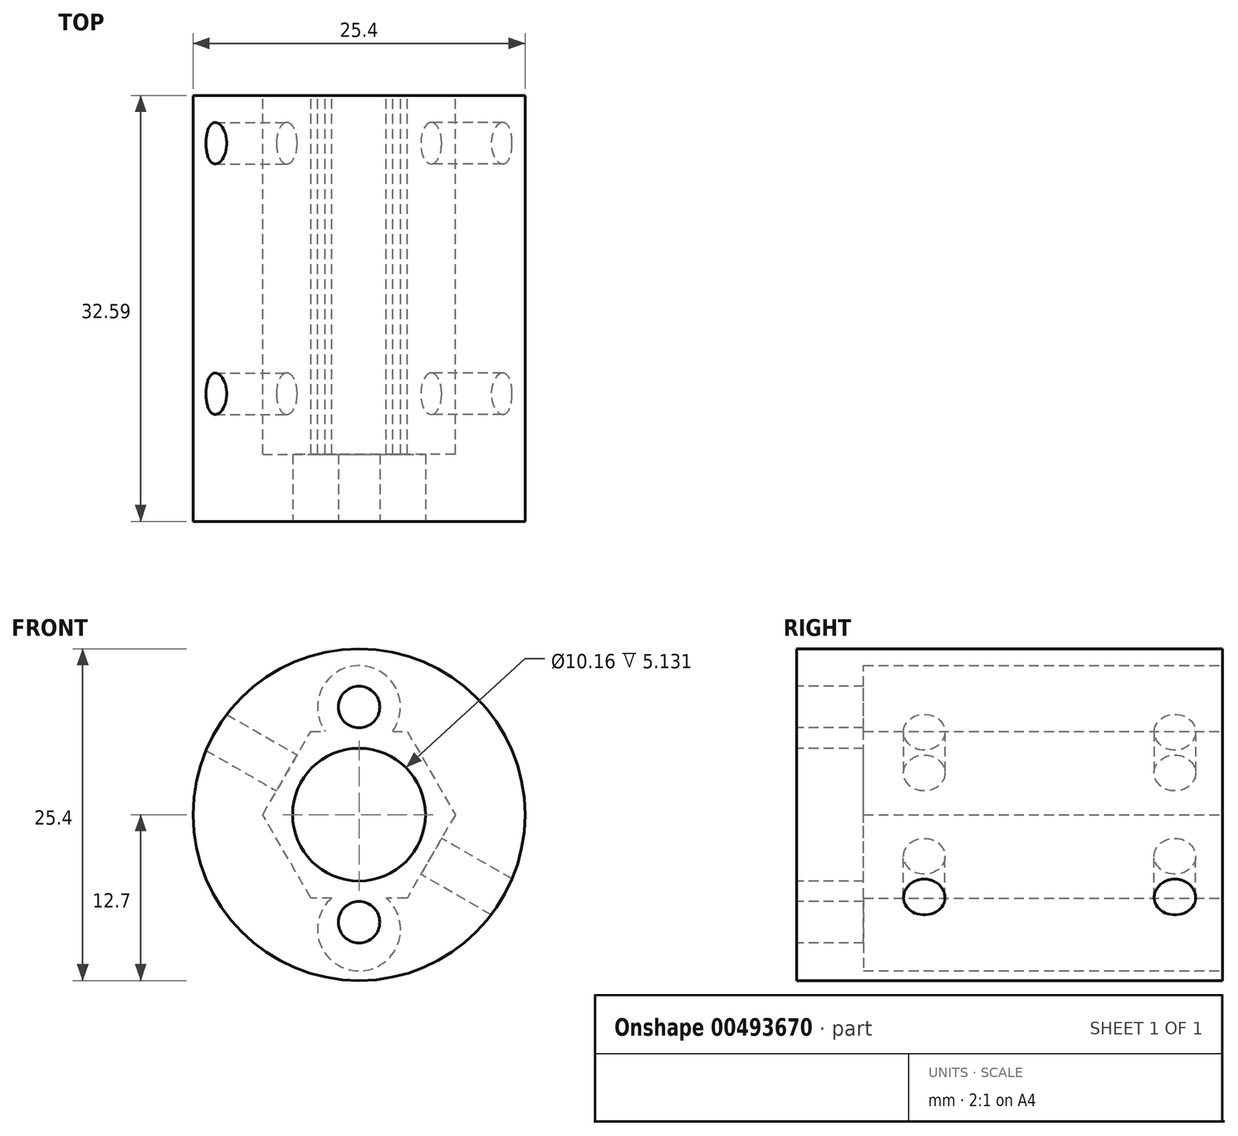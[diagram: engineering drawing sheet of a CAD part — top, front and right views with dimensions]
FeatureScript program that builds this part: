
annotation { "Feature Type Name" : "Feature", "Feature Type Description" : "" }
export const myFeature = defineFeature(function(context is Context, id is Id, definition is map)
    precondition{}
    {
        {
            var Q0;
            Q0=qCreatedBy(makeId("Front.planeOp"),FACE);
            var sketch = newSketch(context, id + "F0", { "sketchPlane" : qUnion([Q0])});
            skCircle(sketch, "E0", {"center": v(0, 0) * mm, "radius": 12.7 * mm});
            skCircle(sketch, "E1.cCircle", {"center": v(0, 0) * mm, "radius": 7.37 * mm, "construction": true});
            skLineSegment(sketch, "E1.0", {"start": v(7.37, 0) * mm, "end": v(3.68, -6.38) * mm});
            skLineSegment(sketch, "E1.1", {"start": v(3.68, -6.38) * mm, "end": v(2.07, -6.38) * mm});
            skLineSegment(sketch, "E1.2", {"start": v(-3.68, -6.38) * mm, "end": v(-7.37, 0) * mm});
            skLineSegment(sketch, "E1.3", {"start": v(-7.37, 0) * mm, "end": v(-3.68, 6.38) * mm});
            skLineSegment(sketch, "E1.4", {"start": v(-3.68, 6.38) * mm, "end": v(-2.58, 6.38) * mm});
            skLineSegment(sketch, "E1.5", {"start": v(3.68, 6.38) * mm, "end": v(7.37, 0) * mm});
            skArc(sketch, "E2", {"start": v(2.58, 6.38) * mm, "mid": v(0, 11.4) * mm, "end": v(-2.58, 6.38) * mm});
            skPoint(sketch, "E2.centerSnap0", {"position": v(0, 6.38) * mm});
            skArc(sketch, "E3.1.0", {"start": v(-2.07, -6.38) * mm, "mid": v(0, -11.96) * mm, "end": v(2.07, -6.38) * mm});
            skPoint(sketch, "E3.center", {"position": v(0, -0.28) * mm});
            skLineSegment(sketch, "E4.trimOffspring", {"start": v(2.58, 6.38) * mm, "end": v(3.68, 6.38) * mm});
            skLineSegment(sketch, "E5.trimOffspring", {"start": v(-2.07, -6.38) * mm, "end": v(-3.68, -6.38) * mm});
            skSolve(sketch);
        }
        {
            var Q0;
            Q0=makeQuery(id+"F0.imprint","IMPRINT",FACE,{"disambiguationData":[TD([[makeQuery(id+"F0.imprint","IMPRINT",EDGE,{"derivedFrom":sQuery(id+"F0.wireOp",EDGE,"E1.0")}),-1.0]])]});
            var Q1;
            Q1=makeQuery(id+"F0.imprint","IMPRINT",FACE,{"disambiguationData":[TD([[makeQuery(id+"F0.imprint","IMPRINT",EDGE,{"derivedFrom":sQuery(id+"F0.wireOp",EDGE,"E0")}),1.0]])]});
            extrude(context, id + "F1", {"entities" : qUnion([Q0, Q1]), "depth" : 25.4 * mm});
        }
        {
            var Q0;
            Q0=makeQuery(id+"F0.imprint","IMPRINT",FACE,{"disambiguationData":[TD([[makeQuery(id+"F0.imprint","IMPRINT",EDGE,{"derivedFrom":sQuery(id+"F0.wireOp",EDGE,"E1.0")}),-1.0]])]});
            extrude(context, id + "F2", {"entities" : qUnion([Q0]), "operationType" : NewBodyOperationType.REMOVE, "depth" : 20.27 * mm, "offsetDistance" : 25.4 * mm});
        }
        {
            var Q0;
            Q0=makeQuery(id+"F1.opExtrude","CAP_FACE",FACE,{"disambiguationData":[OSD([sQuery(id+"F0.wireOp",EDGE,"E0")])],"isStart":false});
            var sketch = newSketch(context, id + "F3", { "sketchPlane" : qUnion([Q0])});
            skSolve(sketch);
        }
        {
            var Q0;
            Q0=makeQuery(id+"F3.imprint","IMPRINT",FACE,{"disambiguationData":[TD([[makeQuery(id+"F3.imprint","IMPRINT",EDGE,{"derivedFrom":makeQuery(id+"F1.opExtrude","CAP_EDGE",EDGE,{"disambiguationData":[OSD([sQuery(id+"F0.wireOp",EDGE,"E0")])],"isStart":false})}),1.0]])]});
            var sketch = newSketch(context, id + "F4", { "sketchPlane" : qUnion([Q0])});
            skCircle(sketch, "E6", {"center": v(0, 8.24) * mm, "radius": 1.59 * mm});
            skCircle(sketch, "E7.1.0", {"center": v(0, -8.24) * mm, "radius": 1.59 * mm});
            skPoint(sketch, "E7.center", {"position": v(0, 0) * mm});
            skSolve(sketch);
        }
        {
            var Q0;
            Q0 = qSketchRegion(id + "F4", true);
            extrude(context, id + "F5", {"entities" : qUnion([Q0]), "operationType" : NewBodyOperationType.REMOVE, "oppositeDirection" : true, "depth" : 19.05 * mm, "offsetDistance" : 25.4 * mm});
        }
        {
            var Q0;
            Q0=makeQuery(id+"F3.imprint","IMPRINT",FACE,{"disambiguationData":[TD([[makeQuery(id+"F3.imprint","IMPRINT",EDGE,{"derivedFrom":makeQuery(id+"F1.opExtrude","CAP_EDGE",EDGE,{"disambiguationData":[OSD([sQuery(id+"F0.wireOp",EDGE,"E0")])],"isStart":false})}),1.0]])]});
            var sketch = newSketch(context, id + "F6", { "sketchPlane" : qUnion([Q0])});
            skCircle(sketch, "E8", {"center": v(0, 0) * mm, "radius": 5.08 * mm});
            skSolve(sketch);
        }
        {
            var Q0;
            Q0 = qSketchRegion(id + "F6", true);
            extrude(context, id + "F7", {"entities" : qUnion([Q0]), "operationType" : NewBodyOperationType.REMOVE, "oppositeDirection" : true, "depth" : 127 * mm, "offsetDistance" : 25.4 * mm});
        }
        {
            var Q0;
            Q0=makeQuery(id+"F2.boolean.opBoolean","COPY",FACE,{"derivedFrom":makeQuery(id+"F2.opExtrude","SWEPT_FACE",FACE,{"disambiguationData":[OSD([sQuery(id+"F0.wireOp",EDGE,"E1.0")])]})});
            var sketch = newSketch(context, id + "F8", { "sketchPlane" : qUnion([Q0])});
            skCircle(sketch, "E9", {"center": v(15.63, 0) * mm, "radius": 1.59 * mm});
            skCircle(sketch, "E10", {"center": v(-3.54, 0) * mm, "radius": 1.59 * mm});
            skSolve(sketch);
        }
        {
            var Q0;
            Q0=makeQuery(id+"F0.imprint","IMPRINT",FACE,{"disambiguationData":[TD([[makeQuery(id+"F0.imprint","IMPRINT",EDGE,{"derivedFrom":sQuery(id+"F0.wireOp",EDGE,"E0")}),1.0]])]});
            extrude(context, id + "F9", {"entities" : qUnion([Q0]), "operationType" : NewBodyOperationType.ADD, "oppositeDirection" : true, "depth" : 7.2 * mm, "offsetDistance" : 25.4 * mm});
        }
        {
            var Q0;
            Q0 = qSketchRegion(id + "F8", true);
            extrude(context, id + "F10", {"entities" : qUnion([Q0]), "operationType" : NewBodyOperationType.REMOVE, "oppositeDirection" : true, "depth" : 127 * mm, "offsetDistance" : 25.4 * mm});
        }
        {
            var Q0;
            Q0 = qSketchRegion(id + "F8", true);
            extrude(context, id + "F11", {"entities" : qUnion([Q0]), "operationType" : NewBodyOperationType.REMOVE, "depth" : 127 * mm, "offsetDistance" : 25.4 * mm});
        }
    });
